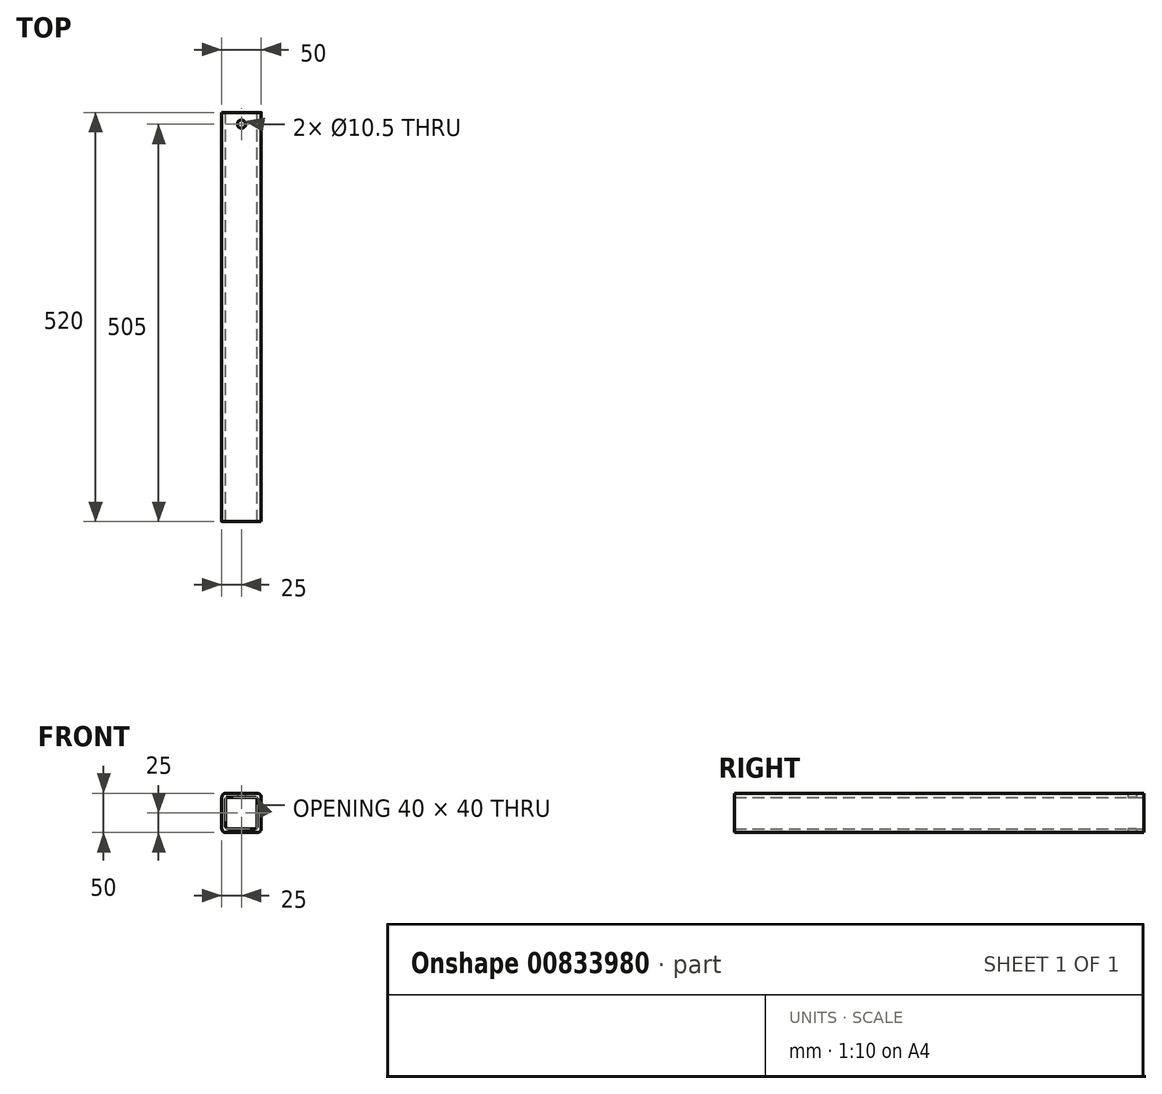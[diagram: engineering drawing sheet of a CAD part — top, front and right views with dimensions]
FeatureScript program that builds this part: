
annotation { "Feature Type Name" : "Feature", "Feature Type Description" : "" }
export const myFeature = defineFeature(function(context is Context, id is Id, definition is map)
    precondition{}
    {
        {
            var Q0;
            Q0=qCreatedBy(makeId("Front.planeOp"),FACE);
            var sketch = newSketch(context, id + "F0", { "sketchPlane" : qUnion([Q0])});
            skLineSegment(sketch, "E0.bottom", {"start": v(25, 25) * mm, "end": v(-25, 25) * mm});
            skLineSegment(sketch, "E0.top", {"start": v(25, -25) * mm, "end": v(-25, -25) * mm});
            skLineSegment(sketch, "E0.left", {"start": v(25, 25) * mm, "end": v(25, -25) * mm});
            skLineSegment(sketch, "E0.right", {"start": v(-25, 25) * mm, "end": v(-25, -25) * mm});
            skPoint(sketch, "E0.middle", {"position": v(0, 0) * mm});
            skLineSegment(sketch, "E1.bottom", {"start": v(20, 20) * mm, "end": v(-20, 20) * mm});
            skLineSegment(sketch, "E1.top", {"start": v(20, -20) * mm, "end": v(-20, -20) * mm});
            skLineSegment(sketch, "E1.left", {"start": v(20, 20) * mm, "end": v(20, -20) * mm});
            skLineSegment(sketch, "E1.right", {"start": v(-20, 20) * mm, "end": v(-20, -20) * mm});
            skSolve(sketch);
        }
        {
            var Q0;
            Q0=makeQuery(id+"F0.imprint","IMPRINT",FACE,{"disambiguationData":[TD([[makeQuery(id+"F0.imprint","IMPRINT",EDGE,{"derivedFrom":sQuery(id+"F0.wireOp",EDGE,"E0.bottom")}),1.0]])]});
            extrude(context, id + "F1", {"entities" : qUnion([Q0]), "depth" : 520 * mm, "offsetDistance" : 25 * mm});
        }
        {
            var Q0;
            Q0=makeQuery(id+"F1.opExtrude","SWEPT_EDGE",EDGE,{"disambiguationData":[OSD([sQuery(id+"F0.wireOp",EDGE,"E0.bottom"),sQuery(id+"F0.wireOp",EDGE,"E0.left")])]});
            var Q1;
            Q1=makeQuery(id+"F1.opExtrude","SWEPT_EDGE",EDGE,{"disambiguationData":[OSD([sQuery(id+"F0.wireOp",EDGE,"E0.bottom"),sQuery(id+"F0.wireOp",EDGE,"E0.right")])]});
            var Q2;
            Q2=makeQuery(id+"F1.opExtrude","SWEPT_EDGE",EDGE,{"disambiguationData":[OSD([sQuery(id+"F0.wireOp",EDGE,"E0.top"),sQuery(id+"F0.wireOp",EDGE,"E0.left")])]});
            var Q3;
            Q3=makeQuery(id+"F1.opExtrude","SWEPT_EDGE",EDGE,{"disambiguationData":[OSD([sQuery(id+"F0.wireOp",EDGE,"E0.top"),sQuery(id+"F0.wireOp",EDGE,"E0.right")])]});
            fillet(context, id + "F2", {"entities" : qUnion([Q0, Q1, Q2, Q3]), "radius" : 5 * mm, "tangentPropagation" : true, "allowEdgeOverflow" : false});
        }
        {
            var Q0;
            Q0=makeQuery(id+"F1.opExtrude","SWEPT_EDGE",EDGE,{"disambiguationData":[OSD([sQuery(id+"F0.wireOp",EDGE,"E1.bottom"),sQuery(id+"F0.wireOp",EDGE,"E1.right")])]});
            var Q1;
            Q1=makeQuery(id+"F1.opExtrude","SWEPT_EDGE",EDGE,{"disambiguationData":[OSD([sQuery(id+"F0.wireOp",EDGE,"E1.bottom"),sQuery(id+"F0.wireOp",EDGE,"E1.left")])]});
            var Q2;
            Q2=makeQuery(id+"F1.opExtrude","SWEPT_EDGE",EDGE,{"disambiguationData":[OSD([sQuery(id+"F0.wireOp",EDGE,"E1.top"),sQuery(id+"F0.wireOp",EDGE,"E1.left")])]});
            var Q3;
            Q3=makeQuery(id+"F1.opExtrude","SWEPT_EDGE",EDGE,{"disambiguationData":[OSD([sQuery(id+"F0.wireOp",EDGE,"E1.top"),sQuery(id+"F0.wireOp",EDGE,"E1.right")])]});
            fillet(context, id + "F3", {"entities" : qUnion([Q0, Q1, Q2, Q3]), "radius" : 3 * mm, "tangentPropagation" : true, "allowEdgeOverflow" : false});
        }
        {
            var Q0;
            Q0=makeQuery(id+"F1.opExtrude","SWEPT_FACE",FACE,{"disambiguationData":[OSD([sQuery(id+"F0.wireOp",EDGE,"E0.top")])]});
            var sketch = newSketch(context, id + "F4", { "sketchPlane" : qUnion([Q0])});
            skPoint(sketch, "E2", {"position": v(0, 15) * mm});
            skSolve(sketch);
        }
        {
            var Q0;
            Q0=sQuery(id+"F4.wireOp",VERTEX,"E2");
            var Q1;
            Q1=makeQuery(id+"F1.opExtrude","SWEPT_BODY",BODY,{"disambiguationData":[OSD([sQuery(id+"F0.wireOp",EDGE,"E0.bottom"),sQuery(id+"F0.wireOp",EDGE,"E0.top"),sQuery(id+"F0.wireOp",EDGE,"E0.left"),sQuery(id+"F0.wireOp",EDGE,"E0.right"),sQuery(id+"F0.wireOp",EDGE,"E1.bottom"),sQuery(id+"F0.wireOp",EDGE,"E1.top"),sQuery(id+"F0.wireOp",EDGE,"E1.left"),sQuery(id+"F0.wireOp",EDGE,"E1.right")])]});
            hole(context, id + "F5", {"style" : HoleStyle.SIMPLE, "endStyle" : HoleEndStyle.THROUGH, "holeDiameter" : 10.5 * mm, "majorDiameter" : 5 * mm, "isTappedThrough" : true, "tappedDepth" : 12 * mm, "tapClearance" : 3, "startFromSketch" : true, "locations" : qUnion([Q0]), "scope" : qUnion([Q1])});
        }
    });
